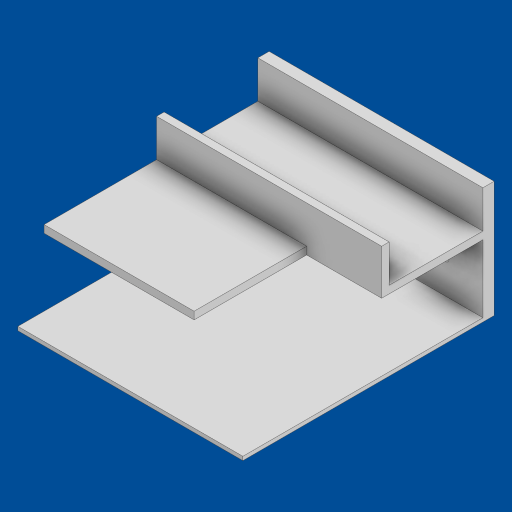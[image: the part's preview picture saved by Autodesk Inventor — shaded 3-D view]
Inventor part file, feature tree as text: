
AUTODESK INVENTOR PART (.ipt)
format: ipt  version: 2023.1 (Build 271208000, 208)  size: 181,248 bytes
history: native  units: mm
features: extrude x5, sketch x4, projected_geometry x2
ambient origin geometry x8: Origin, YZ Plane, XZ Plane, XY Plane, X Axis, Y Axis, Z Axis, Center Point
bodies: Solid1 (feature_tree)
feature tree (11):
  extrude  "Extrusion1"  Depth=60.0mm
  extrude  "Extrusion2"  Depth=20.0mm TaperAngle=0.0deg
  sketch  "Sketch3"  dims[d6=2.0mm d7=0.0mm d8=3.0mm]
  extrude  "Extrusion3"  Depth=3.0mm
  extrude  "Extrusion5"  Depth=2.0mm
  extrude  "Extrusion6"  Depth=10.0mm TaperAngle=0.0deg
  sketch  "Sketch1"  dims[d0=1.0mm d1=0.0mm d2=60.0mm]
  sketch  "Sketch2"  dims[d3=67.0mm d4=20.0mm d5=0.0mm]
  projected_geometry  "Projected Loop1"
  projected_geometry  "Projected Loop2"
  sketch  "Sketch5"  dims[d9=3.0mm d16=2.0mm d17=10.0mm d18=0.0mm d19=25.0mm d20=2.0mm d21=2.0mm d22=40.0mm d23=10.0mm d24=20.0mm d25=0.0mm d26=40.0mm d27=30.0mm]
